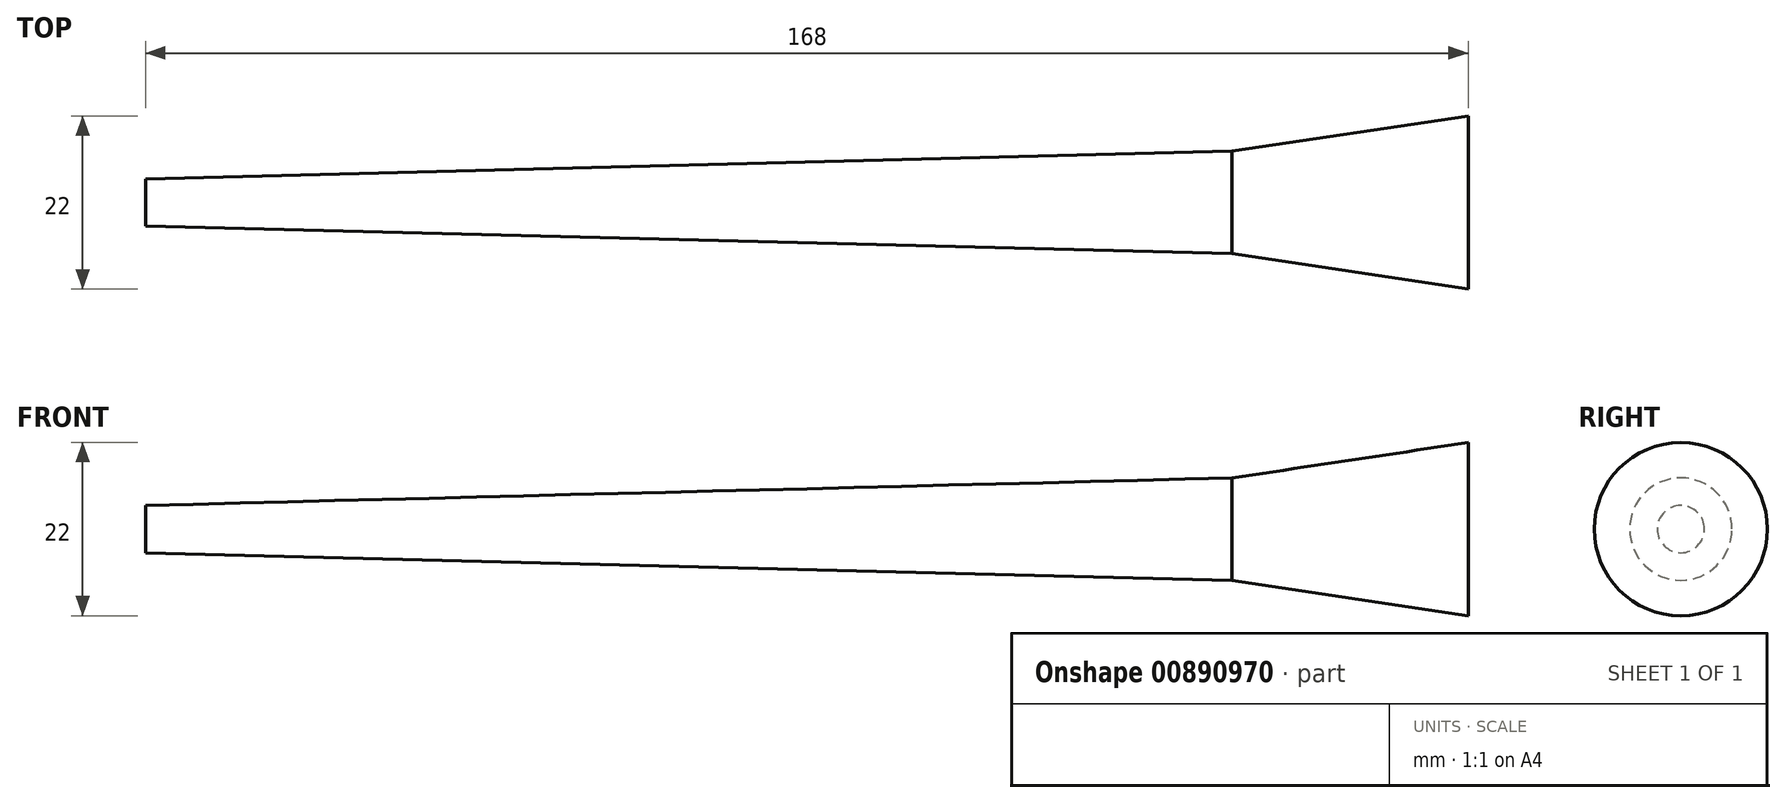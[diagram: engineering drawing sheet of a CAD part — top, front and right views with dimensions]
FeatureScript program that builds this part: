
annotation { "Feature Type Name" : "Feature", "Feature Type Description" : "" }
export const myFeature = defineFeature(function(context is Context, id is Id, definition is map)
    precondition{}
    {
        {
            var Q0;
            Q0=qCreatedBy(makeId("Top.planeOp"),FACE);
            var sketch = newSketch(context, id + "F0", { "sketchPlane" : qUnion([Q0])});
            skLineSegment(sketch, "E0.bottom", {"start": v(-94.05, 0) * mm, "end": v(43.95, 0) * mm});
            skLineSegment(sketch, "E0.left", {"start": v(-94.05, 0) * mm, "end": v(-94.05, 3) * mm});
            skLineSegment(sketch, "E0.right", {"start": v(43.95, 0) * mm, "end": v(43.95, 6.5) * mm});
            skLineSegment(sketch, "E1", {"start": v(-113.5, 0) * mm, "end": v(98.19, 0) * mm});
            skLineSegment(sketch, "E2", {"start": v(43.95, 6.5) * mm, "end": v(73.95, 11) * mm});
            skLineSegment(sketch, "E3", {"start": v(73.95, 11) * mm, "end": v(73.95, 0) * mm});
            skLineSegment(sketch, "E4", {"start": v(73.95, 0) * mm, "end": v(43.95, 0) * mm});
            skLineSegment(sketch, "E5", {"start": v(43.95, 6.5) * mm, "end": v(-94.05, 3) * mm});
            skPoint(sketch, "E0.top.start.orphan", {"position": v(-94.05, 6) * mm});
            skSolve(sketch);
        }
        {
            var Q0;
            Q0=qSketchRegion(id+"F0",true);
            var Q1;
            Q1=sQuery(id+"F0.wireOp",EDGE,"E1");
            revolve(context, id + "F1", {"surfaceOperationType" : NewSurfaceOperationType.NEW, "entities" : qUnion([Q0]), "axis" : qUnion([Q1]), "revolveType" : RevolveType.FULL});
        }
    });
